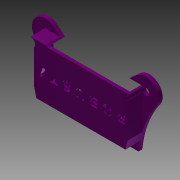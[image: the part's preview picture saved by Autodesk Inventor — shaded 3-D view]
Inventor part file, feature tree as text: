
AUTODESK INVENTOR PART (.ipt)
format: ipt  version: 2015 (Build 190159000, 159)  size: 642,048 bytes
history: native  units: mm
features: extrude x17, sketch x10, fillet x6, projected_geometry x5, plane x2
ambient origin geometry x8: Origin, YZ Plane, XZ Plane, XY Plane, X Axis, Y Axis, Z Axis, Center Point
bodies: Solid1 (feature_tree)
feature tree (40):
  extrude  "Extrusion1"  Depth=1.0mm
  extrude  "Extrusion2"  Depth=1.0mm
  extrude  "Extrusion3"  Depth=3.5mm TaperAngle=0.0deg
  extrude  "Extrusion4"  Depth=13.5mm TaperAngle=0.0deg
  extrude  "Extrusion5"  Depth=13.5mm TaperAngle=0.0deg
  extrude  "Extrusion6"  Depth=13.5mm TaperAngle=0.0deg
  extrude  "Extrusion7"  Depth=13.5mm TaperAngle=0.0deg
  extrude  "Extrusion8"  Depth=13.5mm TaperAngle=0.0deg
  plane  "Work Plane1"
  extrude  "Extrusion9"  Depth=13.5mm TaperAngle=0.0deg
  extrude  "Extrusion10"  Depth=3.5mm TaperAngle=0.0deg
  extrude  "Extrusion11"  Depth=3.5mm TaperAngle=0.0deg
  fillet  "Fillet1"  Radius=3.5mm
  fillet  "Fillet2"  Radius=1.0mm
  fillet  "Fillet3"  Radius=1.0mm
  fillet  "Fillet4"  Radius=1.0mm
  fillet  "Fillet5"  Radius=1.0mm
  fillet  "Fillet6"  Radius=1.0mm
  plane  "Work Plane2"
  extrude  "Extrusion12"  Depth=10.0mm
  extrude  "Extrusion13"  TaperAngle=0.0deg  [1 undecoded]
  sketch  "Sketch18"  dims[d18=13.5mm d19=0.0mm d20=13.5mm d21=0.0mm]
  extrude  "Extrusion16"  Depth=10.0mm
  extrude  "Extrusion18"  TaperAngle=90.0deg  [1 undecoded]
  extrude  "Extrusion19"  TaperAngle=45.0deg  [1 undecoded]
  extrude  "Extrusion20"  Depth=10.0mm TaperAngle=0.0deg
  sketch  "Sketch6"  dims[d0=1.0mm d1=1.0mm]
  sketch  "Sketch7"  dims[d2=1.0mm d3=1.0mm]
  sketch  "Sketch10"  dims[d4=1.0mm d6=3.5mm d7=0.0mm]
  sketch  "Sketch11"  dims[d9=180.0deg d10=13.5mm d11=0.0mm]
  projected_geometry  "Projected Loop1"
  sketch  "Sketch12"  dims[d12=90.0deg d13=13.5mm d14=0.0mm]
  projected_geometry  "Projected Loop2"
  sketch  "Sketch15"  dims[d15=90.0deg d16=13.5mm d17=0.0mm]
  projected_geometry  "Projected Loop4"
  projected_geometry  "Projected Loop5"
  projected_geometry  "Projected Loop6"
  sketch  "Sketch19"  dims[d22=1.0mm d23=13.5mm d24=0.0mm]
  sketch  "Sketch20"  dims[d25=1.0mm d26=13.5mm d27=0.0mm]
  sketch  "Sketch23"  dims[d28=-13.5mm d29=3.5mm d30=0.0mm d31=3.5mm d32=0.0mm d33=3.5mm d34=0.0mm d35=1.0mm d38=1.0mm d39=1.0mm d40=1.0mm d41=1.0mm d42=1.0mm d43=0.0mm d44=4.125mm d45=90.0deg d46=45.0deg d47=50.0mm d48=0.0mm d49=3.178712mm d50=26.452487mm d51=50.0mm d52=0.0mm d61=90.0deg d64=1.0mm d65=1.0mm d68=1.0mm d69=1.0mm d73=3.5mm d74=0.0mm d83=0.25mm d84=0.25mm d85=0.25mm d86=3.5mm d87=0.0mm d90=0.75mm d91=3.5mm d92=0.0mm d98=6.5mm d99=6.5mm d100=10.0mm d101=0.0mm]
note: 3 required parameter values undecoded (feature->parameter linkage not recoverable at this tier; creation-order binding heuristic only, values carry confidence <= 0.55)
